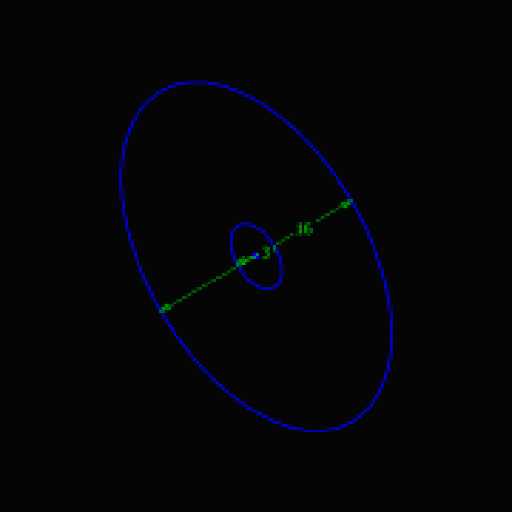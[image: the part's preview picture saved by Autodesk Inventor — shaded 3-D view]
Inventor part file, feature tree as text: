
AUTODESK INVENTOR PART (.ipt)
format: ipt  version: 2023.2 (Build 272271030, 271C)  size: 83,456 bytes
history: native  units: mm
features: extrude x1, sketch x1
ambient origin geometry x8: Origin, YZ Plane, XZ Plane, XY Plane, X Axis, Y Axis, Z Axis, Center Point
bodies: Solid1 (feature_tree)
feature tree (2):
  extrude  "Extrusion1"  Depth=5.0mm
  sketch  "Sketch1"  dims[d0=3.0mm d1=16.0mm d2=5.0mm d3=0.0mm]
